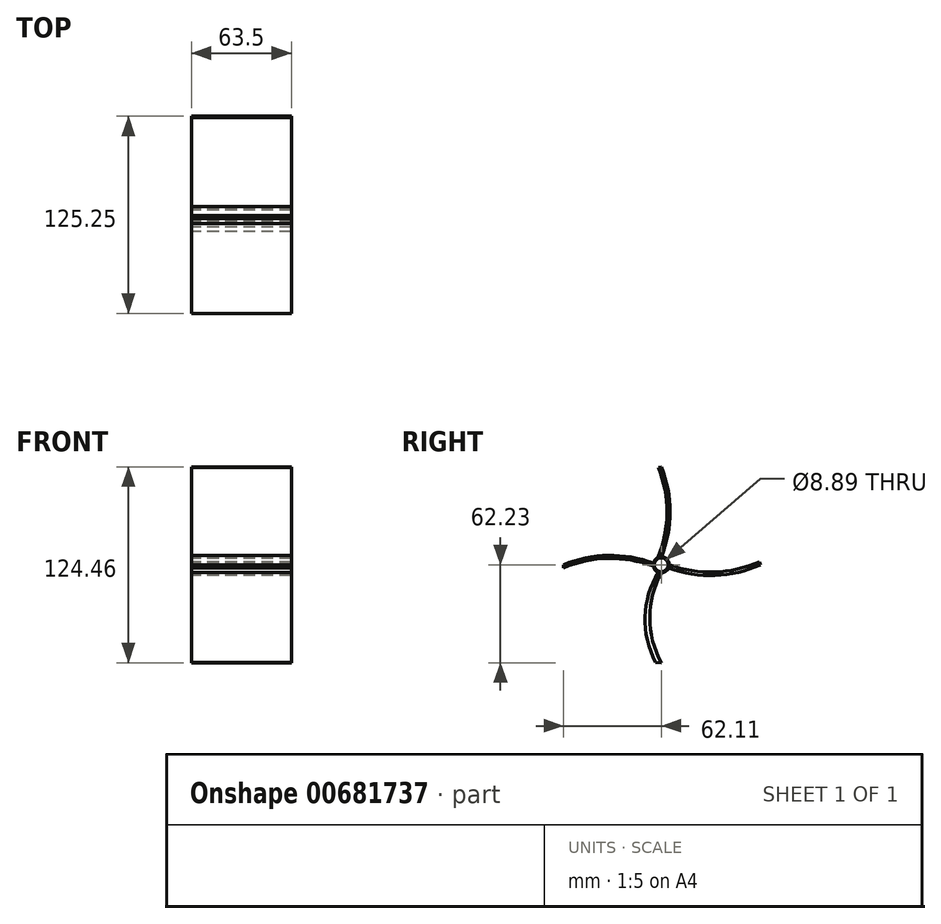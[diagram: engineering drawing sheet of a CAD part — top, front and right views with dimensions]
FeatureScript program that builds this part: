
annotation { "Feature Type Name" : "Feature", "Feature Type Description" : "" }
export const myFeature = defineFeature(function(context is Context, id is Id, definition is map)
    precondition{}
    {
        {
            var Q0;
            Q0=qCreatedBy(makeId("Right.planeOp"),FACE);
            var sketch = newSketch(context, id + "F0", { "sketchPlane" : qUnion([Q0])});
            skCircle(sketch, "E0", {"center": v(0, 0) * mm, "radius": 4.45 * mm});
            skSolve(sketch);
        }
        {
            var Q0;
            Q0=qCreatedBy(makeId("Right.planeOp"),FACE);
            var sketch = newSketch(context, id + "F1", { "sketchPlane" : qUnion([Q0])});
            skCircle(sketch, "E1", {"center": v(0, 0) * mm, "radius": 5.08 * mm});
            skSolve(sketch);
        }
        {
            var Q0;
            Q0 = qSketchRegion(id + "F1", true);
            extrude(context, id + "F2", {"entities" : qUnion([Q0]), "depth" : 63.5 * mm, "offsetDistance" : 25.4 * mm});
        }
        {
            var Q0;
            Q0 = qSketchRegion(id + "F0", true);
            extrude(context, id + "F3", {"entities" : qUnion([Q0]), "operationType" : NewBodyOperationType.REMOVE, "depth" : 63.5 * mm, "offsetDistance" : 25.4 * mm});
        }
        {
            var Q0;
            Q0=makeQuery(id+"F2.opExtrude","CAP_FACE",FACE,{"disambiguationData":[OSD([sQuery(id+"F1.wireOp",EDGE,"E1")])],"isStart":true});
            var sketch = newSketch(context, id + "F4", { "sketchPlane" : qUnion([Q0])});
            skArc(sketch, "E2", {"start": v(0, 62.23) * mm, "mid": v(-5.56, 33.65) * mm, "end": v(0, 5.08) * mm});
            skArc(sketch, "E3", {"start": v(1.86, 61.81) * mm, "mid": v(-3.62, 33.22) * mm, "end": v(2.02, 4.66) * mm});
            skLineSegment(sketch, "E4", {"start": v(0, 5.08) * mm, "end": v(2.02, 4.66) * mm});
            skLineSegment(sketch, "E5", {"start": v(1.86, 61.81) * mm, "end": v(0, 62.23) * mm});
            skArc(sketch, "E6", {"start": v(-62.23, 1.9) * mm, "mid": v(-33.84, -4.61) * mm, "end": v(-5.08, 0) * mm});
            skLineSegment(sketch, "E7", {"start": v(-62.23, 0) * mm, "end": v(-62.23, 1.9) * mm});
            skLineSegment(sketch, "E8", {"start": v(-5.08, 0) * mm, "end": v(-5.08, 0) * mm});
            skArc(sketch, "E9", {"start": v(62.14, 0) * mm, "mid": v(33.66, 6.04) * mm, "end": v(4.99, 0.95) * mm});
            skArc(sketch, "E10", {"start": v(62.14, -1.9) * mm, "mid": v(33.66, 4.13) * mm, "end": v(4.99, -0.95) * mm});
            skLineSegment(sketch, "E11", {"start": v(62.14, -1.9) * mm, "end": v(62.14, 0) * mm});
            skArc(sketch, "E12", {"start": v(-63.14, 0) * mm, "mid": v(-34.12, -6.8) * mm, "end": v(-4.71, -1.9) * mm});
            skLineSegment(sketch, "E13", {"start": v(-63.14, 0) * mm, "end": v(-62.23, 1.9) * mm});
            skLineSegment(sketch, "E14", {"start": v(-5.08, 0) * mm, "end": v(-4.71, -1.9) * mm});
            skSolve(sketch);
        }
        {
            var Q0;
            Q0 = qSketchRegion(id + "F4", true);
            extrude(context, id + "F5", {"entities" : qUnion([Q0]), "operationType" : NewBodyOperationType.ADD, "oppositeDirection" : true, "depth" : 63.5 * mm, "offsetDistance" : 25.4 * mm});
        }
        {
            var Q0;
            Q0=makeQuery(id+"F5.boolean.opBoolean","MERGE",FACE,{"derivedFrom":[makeQuery(id+"F2.opExtrude","CAP_FACE",FACE,{"disambiguationData":[OSD([sQuery(id+"F1.wireOp",EDGE,"E1")])],"isStart":true}),makeQuery(id+"F5.opExtrude","CAP_FACE",FACE,{"disambiguationData":[OSD([sQuery(id+"F4.wireOp",EDGE,"E2"),sQuery(id+"F4.wireOp",EDGE,"E3"),sQuery(id+"F4.wireOp",EDGE,"E4"),sQuery(id+"F4.wireOp",EDGE,"E5")])],"isStart":true}),makeQuery(id+"F5.opExtrude","CAP_FACE",FACE,{"disambiguationData":[OSD([sQuery(id+"F4.wireOp",EDGE,"D8GLxEXb-62b8-rBnE-rhaD-LPeKhwrKpIia"),sQuery(id+"F4.wireOp",EDGE,"E6"),sQuery(id+"F4.wireOp",EDGE,"E7"),sQuery(id+"F4.wireOp",EDGE,"E8")])],"isStart":true})]});
            var sketch = newSketch(context, id + "F6", { "sketchPlane" : qUnion([Q0])});
            skArc(sketch, "E15", {"start": v(3.54, -61.87) * mm, "mid": v(10.3, -33.08) * mm, "end": v(1.87, -4.72) * mm});
            skPoint(sketch, "E15.startSnap0", {"position": v(3.54, -3.64) * mm});
            skArc(sketch, "E16", {"start": v(0, -62.23) * mm, "mid": v(7.22, -33.66) * mm, "end": v(0, -5.08) * mm});
            skLineSegment(sketch, "E17", {"start": v(1.87, -4.72) * mm, "end": v(0, -5.08) * mm});
            skLineSegment(sketch, "E18", {"start": v(3.54, -61.87) * mm, "end": v(0, -62.23) * mm});
            skSolve(sketch);
        }
        {
            var Q0;
            Q0 = qSketchRegion(id + "F6", true);
            extrude(context, id + "F7", {"entities" : qUnion([Q0]), "operationType" : NewBodyOperationType.ADD, "oppositeDirection" : true, "depth" : 63.5 * mm, "offsetDistance" : 25.4 * mm});
        }
        {
            var Q0;
            Q0 = qSketchRegion(id + "F4", true);
            extrude(context, id + "F8", {"entities" : qUnion([Q0]), "operationType" : NewBodyOperationType.ADD, "oppositeDirection" : true, "depth" : 63.5 * mm, "offsetDistance" : 25.4 * mm});
        }
        {
            var Q0;
            Q0 = qSketchRegion(id + "F4", true);
            extrude(context, id + "F9", {"entities" : qUnion([Q0]), "operationType" : NewBodyOperationType.ADD, "oppositeDirection" : true, "depth" : 63.5 * mm, "offsetDistance" : 25.4 * mm});
        }
        {
            var Q0;
            Q0 = qSketchRegion(id + "F4", true);
            extrude(context, id + "F10", {"entities" : qUnion([Q0]), "operationType" : NewBodyOperationType.ADD, "oppositeDirection" : true, "depth" : 63.5 * mm, "offsetDistance" : 25.4 * mm});
        }
        {
            var Q0;
            {var subQ1=sQuery(id+"F4.wireOp",EDGE,"E4");Q0=makeQuery(id+"F4.imprint","IMPRINT",FACE,{"disambiguationData":[TD([[makeQuery(id+"F4.imprint","IMPRINT",EDGE,{"derivedFrom":subQ1}),-1.0]])]});}
            var sketch = newSketch(context, id + "F11", { "sketchPlane" : qUnion([Q0])});
            skArc(sketch, "E19", {"start": v(62.11, 0) * mm, "mid": v(33.64, 5.98) * mm, "end": v(4.96, 1.07) * mm});
            skArc(sketch, "E20", {"start": v(62.11, -1.9) * mm, "mid": v(33.64, 4.02) * mm, "end": v(4.96, -0.84) * mm});
            skLineSegment(sketch, "E21", {"start": v(62.11, -1.9) * mm, "end": v(62.11, 0) * mm});
            skLineSegment(sketch, "E22", {"start": v(4.96, -0.84) * mm, "end": v(4.96, 1.07) * mm});
            skSolve(sketch);
        }
        {
            var Q0;
            Q0 = qSketchRegion(id + "F11", true);
            extrude(context, id + "F12", {"entities" : qUnion([Q0]), "operationType" : NewBodyOperationType.ADD, "oppositeDirection" : true, "depth" : 63.5 * mm, "offsetDistance" : 25.4 * mm});
        }
    });
